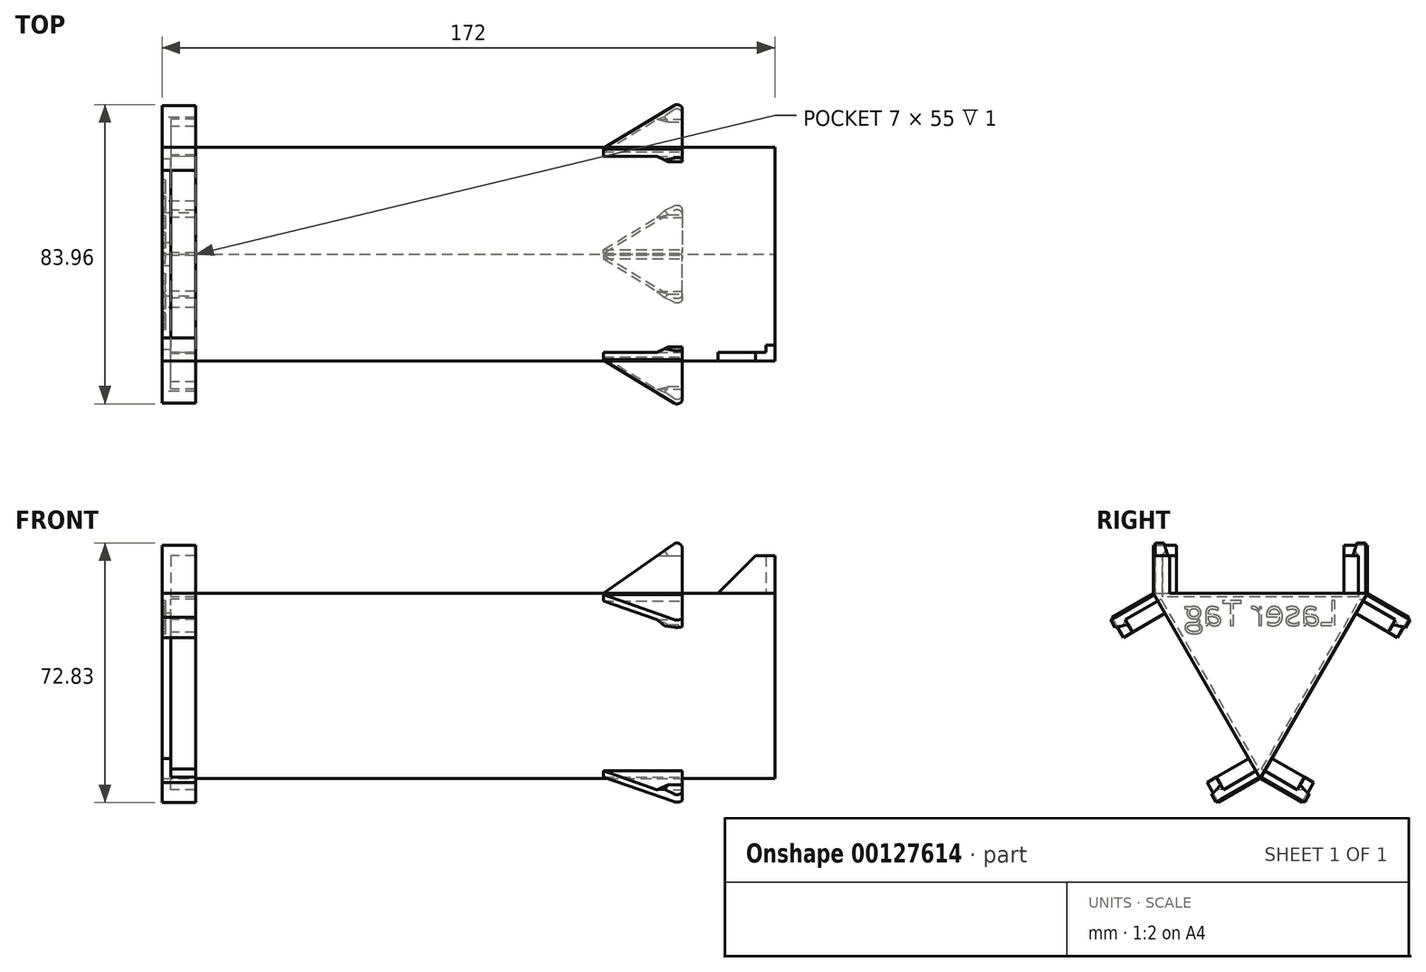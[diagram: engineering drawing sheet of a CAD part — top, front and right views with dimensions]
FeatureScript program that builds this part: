
annotation { "Feature Type Name" : "Feature", "Feature Type Description" : "" }
export const myFeature = defineFeature(function(context is Context, id is Id, definition is map)
    precondition{}
    {
        {
            var Q0;
            Q0=qCreatedBy(makeId("Top.planeOp"),FACE);
            var sketch = newSketch(context, id + "F0", { "sketchPlane" : qUnion([Q0])});
            skLineSegment(sketch, "E0.bottom", {"start": v(83.5, -27.5) * mm, "end": v(-83.5, -27.5) * mm, "construction": true});
            skLineSegment(sketch, "E0.top", {"start": v(83.5, 27.5) * mm, "end": v(-83.5, 27.5) * mm, "construction": true});
            skLineSegment(sketch, "E0.left", {"start": v(83.5, -27.5) * mm, "end": v(83.5, 27.5) * mm, "construction": true});
            skLineSegment(sketch, "E0.right", {"start": v(-83.5, -27.5) * mm, "end": v(-83.5, 27.5) * mm, "construction": true});
            skPoint(sketch, "E0.middle", {"position": v(0, 0) * mm});
            skLineSegment(sketch, "E1.bottom", {"start": v(86, -30) * mm, "end": v(-86, -30) * mm});
            skLineSegment(sketch, "E1.top", {"start": v(86, 0) * mm, "end": v(-86, 0) * mm});
            skLineSegment(sketch, "E1.left", {"start": v(86, -30) * mm, "end": v(86, 0) * mm});
            skLineSegment(sketch, "E1.right", {"start": v(-86, -30) * mm, "end": v(-86, 0) * mm});
            skPoint(sketch, "E1.middle", {"position": v(0, -15) * mm});
            skLineSegment(sketch, "E2", {"start": v(-83.5, -27.5) * mm, "end": v(-83.5, -30) * mm, "construction": true});
            skLineSegment(sketch, "E3", {"start": v(-83.5, -27.5) * mm, "end": v(-86, -27.5) * mm, "construction": true});
            skSolve(sketch);
        }
        {
            var Q0;
            Q0=qCreatedBy(makeId("Right.planeOp"),FACE);
            var Q1;
            Q1=sQuery(id+"F0.wireOp",VERTEX,"E1.top.start");
            cPlane(context, id + "F1", {"entities" : qUnion([Q0, Q1]), "cplaneType" : CPlaneType.PLANE_POINT, "offset" : 25 * mm, "width" : 150 * mm, "height" : 150 * mm});
        }
        {
            var Q0;
            Q0=qCreatedBy(id+"F1.planeOp",FACE);
            var sketch = newSketch(context, id + "F2", { "sketchPlane" : qUnion([Q0])});
            skCircle(sketch, "E4.cCircle", {"center": v(0, -17.32) * mm, "radius": 34.64 * mm, "construction": true});
            skLineSegment(sketch, "E4.0", {"start": v(30, 0) * mm, "end": v(0, -51.96) * mm});
            skLineSegment(sketch, "E4.1", {"start": v(0, -51.96) * mm, "end": v(-30, 0) * mm});
            skLineSegment(sketch, "E4.2", {"start": v(-30, 0) * mm, "end": v(30, 0) * mm});
            skLineSegment(sketch, "E5.0", {"start": v(-27.4, -1.5) * mm, "end": v(0, -1.5) * mm, "construction": true});
            skLineSegment(sketch, "E5.1", {"start": v(0, -48.96) * mm, "end": v(-13.7, -25.23) * mm, "construction": true});
            skLineSegment(sketch, "E5.2", {"start": v(27.4, -1.5) * mm, "end": v(0, -48.96) * mm, "construction": true});
            skLineSegment(sketch, "E6", {"start": v(0, -1.5) * mm, "end": v(-13.7, -25.23) * mm, "construction": true});
            skLineSegment(sketch, "E7", {"start": v(0, -1.5) * mm, "end": v(27.4, -1.5) * mm, "construction": true});
            skLineSegment(sketch, "E8", {"start": v(-13.7, -25.23) * mm, "end": v(-27.4, -1.5) * mm, "construction": true});
            skLineSegment(sketch, "E9", {"start": v(-13.7, -25.23) * mm, "end": v(-13.7, -9.41) * mm, "construction": true});
            skLineSegment(sketch, "E10", {"start": v(-27.4, -1.5) * mm, "end": v(-13.7, -9.41) * mm, "construction": true});
            skLineSegment(sketch, "E11", {"start": v(-13.7, -9.41) * mm, "end": v(-6.85, -13.37) * mm, "construction": true});
            skLineSegment(sketch, "E12", {"start": v(-13.7, -9.41) * mm, "end": v(-13.7, -1.5) * mm, "construction": true});
            skLineSegment(sketch, "E13", {"start": v(-27.4, -1.5) * mm, "end": v(-28.27, 0) * mm, "construction": true});
            skSolve(sketch);
        }
        {
            var Q0;
            Q0=qCreatedBy(makeId("Top.planeOp"),FACE);
            var Q1;
            Q1=sQuery(id+"F2.wireOp",VERTEX,"E4.cCircle.center");
            cPlane(context, id + "F3", {"entities" : qUnion([Q0, Q1]), "cplaneType" : CPlaneType.PLANE_POINT, "offset" : 25 * mm, "width" : 150 * mm, "height" : 150 * mm});
        }
        {
            var Q0;
            Q0=qCreatedBy(id+"F3.planeOp",FACE);
            var sketch = newSketch(context, id + "F4", { "sketchPlane" : qUnion([Q0])});
            skPoint(sketch, "E14.0", {"position": v(86, 0) * mm});
            skPoint(sketch, "E14.1", {"position": v(-86, 0) * mm});
            skLineSegment(sketch, "E15", {"start": v(86, 0) * mm, "end": v(-86, 0) * mm, "construction": true});
            skSolve(sketch);
        }
        {
            var Q0;
            Q0=qCreatedBy(makeId("Right.planeOp"),FACE);
            var Q1;
            Q1=sQuery(id+"F0.wireOp",VERTEX,"E1.top.end");
            cPlane(context, id + "F5", {"entities" : qUnion([Q0, Q1]), "cplaneType" : CPlaneType.PLANE_POINT, "offset" : 25 * mm, "width" : 150 * mm, "height" : 150 * mm});
        }
        {
            var Q0;
            Q0=makeQuery(id+"F2.imprint","IMPRINT",FACE,{"disambiguationData":[TD([[makeQuery(id+"F2.imprint","IMPRINT",EDGE,{"derivedFrom":sQuery(id+"F2.wireOp",EDGE,"E4.0")}),-1.0]])]});
            var Q1;
            Q1=qCreatedBy(id+"F5.planeOp",FACE);
            extrude(context, id + "F6", {"entities" : qUnion([Q0]), "endBound" : BoundingType.UP_TO_SURFACE, "oppositeDirection" : true, "endBoundEntityFace" : qUnion([Q1]), "depth" : 25 * mm});
        }
        {
            var Q0;
            Q0=makeQuery(id+"F6.opExtrude","SWEPT_FACE",FACE,{"disambiguationData":[OSD([sQuery(id+"F2.wireOp",EDGE,"E4.2")])]});
            var sketch = newSketch(context, id + "F7", { "sketchPlane" : qUnion([Q0])});
            skPoint(sketch, "E16.0", {"position": v(-83.5, -27.5) * mm});
            skPoint(sketch, "E17.0", {"position": v(83.5, -27.5) * mm});
            skLineSegment(sketch, "E18", {"start": v(-83.5, -27.5) * mm, "end": v(-83.5, -23.5) * mm});
            skLineSegment(sketch, "E19", {"start": v(-83.5, -23.5) * mm, "end": v(-86, -23.5) * mm});
            skLineSegment(sketch, "E20", {"start": v(-86, -23.5) * mm, "end": v(-86, -30) * mm});
            skLineSegment(sketch, "E21", {"start": v(-86, -30) * mm, "end": v(-76.5, -30) * mm});
            skLineSegment(sketch, "E22", {"start": v(-76.5, -30) * mm, "end": v(-76.5, -27.5) * mm});
            skLineSegment(sketch, "E23", {"start": v(-76.5, -27.5) * mm, "end": v(-83.5, -27.5) * mm});
            skLineSegment(sketch, "E24.bottom", {"start": v(83.5, -27.5) * mm, "end": v(80.5, -27.5) * mm});
            skLineSegment(sketch, "E24.top", {"start": v(86, -30) * mm, "end": v(80.5, -30) * mm});
            skLineSegment(sketch, "E24.right", {"start": v(80.5, -27.5) * mm, "end": v(80.5, -30) * mm});
            skLineSegment(sketch, "E25", {"start": v(83.5, -27.5) * mm, "end": v(83.5, -25.5) * mm});
            skLineSegment(sketch, "E26", {"start": v(83.5, -25.5) * mm, "end": v(86, -25.5) * mm});
            skLineSegment(sketch, "E27", {"start": v(86, -25.5) * mm, "end": v(86, -30) * mm});
            skSolve(sketch);
        }
        {
            var Q0;
            Q0=qSketchRegion(id+"F7",true);
            extrude(context, id + "F8", {"entities" : qUnion([Q0]), "depth" : 10.5 * mm});
        }
        {
            var Q0;
            Q0=makeQuery(id+"F8.opExtrude","CAP_FACE",FACE,{"disambiguationData":[OSD([sQuery(id+"F7.wireOp",EDGE,"E18"),sQuery(id+"F7.wireOp",EDGE,"E19"),sQuery(id+"F7.wireOp",EDGE,"E20"),sQuery(id+"F7.wireOp",EDGE,"E21"),sQuery(id+"F7.wireOp",EDGE,"E22"),sQuery(id+"F7.wireOp",EDGE,"E23")])],"isStart":false});
            var sketch = newSketch(context, id + "F9", { "sketchPlane" : qUnion([Q0])});
            skLineSegment(sketch, "E28.bottom", {"start": v(-86, -23.5) * mm, "end": v(-76.5, -23.5) * mm});
            skLineSegment(sketch, "E28.top", {"start": v(-86, -30) * mm, "end": v(-76.5, -30) * mm});
            skLineSegment(sketch, "E28.left", {"start": v(-86, -23.5) * mm, "end": v(-86, -30) * mm});
            skLineSegment(sketch, "E28.right", {"start": v(-76.5, -23.5) * mm, "end": v(-76.5, -30) * mm});
            skSolve(sketch);
        }
        {
            var Q0;
            Q0=qSketchRegion(id+"F9",true);
            extrude(context, id + "F10", {"entities" : qUnion([Q0]), "operationType" : NewBodyOperationType.ADD, "depth" : 3 * mm});
        }
        {
            var Q0;
            Q0=makeQuery(id+"F8.opExtrude","SWEPT_FACE",FACE,{"disambiguationData":[OSD([sQuery(id+"F7.wireOp",EDGE,"E24.top")])]});
            var sketch = newSketch(context, id + "F11", { "sketchPlane" : qUnion([Q0])});
            skLineSegment(sketch, "E29.0", {"start": v(80.5, 10.5) * mm, "end": v(80.5, 0) * mm});
            skLineSegment(sketch, "E30", {"start": v(80.5, 10.5) * mm, "end": v(70, 0) * mm});
            skLineSegment(sketch, "E31", {"start": v(70, 0) * mm, "end": v(80.5, 0) * mm});
            skSolve(sketch);
        }
        {
            var Q0;
            Q0=qSketchRegion(id+"F11",true);
            var Q1;
            Q1=makeQuery(id+"F8.opExtrude","SWEPT_FACE",FACE,{"disambiguationData":[OSD([sQuery(id+"F7.wireOp",EDGE,"E24.bottom")])]});
            extrude(context, id + "F12", {"entities" : qUnion([Q0]), "operationType" : NewBodyOperationType.ADD, "endBound" : BoundingType.UP_TO_SURFACE, "oppositeDirection" : true, "endBoundEntityFace" : qUnion([Q1]), "depth" : 25 * mm});
        }
        {
            var Q0;
            Q0=qCreatedBy(makeId("Front.planeOp"),FACE);
            var Q1;
            Q1=sQuery(id+"F0.wireOp",VERTEX,"E0.left.start");
            cPlane(context, id + "F13", {"entities" : qUnion([Q0, Q1]), "cplaneType" : CPlaneType.PLANE_POINT, "offset" : 25 * mm, "width" : 150 * mm, "height" : 150 * mm});
        }
        {
            var Q0;
            Q0=qCreatedBy(id+"F13.planeOp",FACE);
            var sketch = newSketch(context, id + "F14", { "sketchPlane" : qUnion([Q0])});
            skLineSegment(sketch, "E32.0", {"start": v(83.5, 0) * mm, "end": v(-83.5, 0) * mm, "construction": true});
            skLineSegment(sketch, "E33", {"start": v(37.86, 0) * mm, "end": v(60, 0) * mm});
            skLineSegment(sketch, "E34.0", {"start": v(70, 0) * mm, "end": v(80.5, 10.5) * mm, "construction": true});
            skLineSegment(sketch, "E35", {"start": v(37.86, 0) * mm, "end": v(60, 15.5) * mm});
            skLineSegment(sketch, "E36", {"start": v(60, 15.5) * mm, "end": v(60, 0) * mm});
            skLineSegment(sketch, "E37", {"start": v(80.5, 10.5) * mm, "end": v(60, 10.5) * mm, "construction": true});
            skSolve(sketch);
        }
        {
            var Q0;
            Q0=qSketchRegion(id+"F14",true);
            extrude(context, id + "F15", {"entities" : qUnion([Q0]), "depth" : 2 * mm});
        }
        {
            var Q0;
            Q0=makeQuery(id+"F15.opExtrude","SWEPT_FACE",FACE,{"disambiguationData":[OSD([sQuery(id+"F14.wireOp",EDGE,"E36")])]});
            var sketch = newSketch(context, id + "F16", { "sketchPlane" : qUnion([Q0])});
            skLineSegment(sketch, "E38.0", {"start": v(-27.5, 15.5) * mm, "end": v(-27.5, 0) * mm, "construction": true});
            skLineSegment(sketch, "E39", {"start": v(-27.5, 15.5) * mm, "end": v(-26, 10.5) * mm});
            skLineSegment(sketch, "E40", {"start": v(-26, 10.5) * mm, "end": v(-27.5, 10.5) * mm});
            skPoint(sketch, "E41.0", {"position": v(-27.5, 10.5) * mm});
            skLineSegment(sketch, "E42", {"start": v(-27.5, 10.5) * mm, "end": v(-27.5, 15.5) * mm});
            skSolve(sketch);
        }
        {
            var Q0;
            Q0=qSketchRegion(id+"F16",true);
            var Q1;
            Q1=makeQuery(id+"F15.opExtrude","SWEPT_FACE",FACE,{"disambiguationData":[OSD([sQuery(id+"F14.wireOp",EDGE,"E35")])]});
            extrude(context, id + "F17", {"entities" : qUnion([Q0]), "operationType" : NewBodyOperationType.ADD, "endBound" : BoundingType.UP_TO_SURFACE, "oppositeDirection" : true, "endBoundEntityFace" : qUnion([Q1]), "depth" : 25 * mm});
        }
        {
            var Q0;
            Q0=makeQuery(id+"F17.opExtrude","SWEPT_FACE",FACE,{"disambiguationData":[OSD([sQuery(id+"F16.wireOp",EDGE,"E40")])]});
            var sketch = newSketch(context, id + "F18", { "sketchPlane" : qUnion([Q0])});
            skLineSegment(sketch, "E43.0.0", {"start": v(52.86, 27.5) * mm, "end": v(52.86, 26) * mm, "construction": true});
            skLineSegment(sketch, "E43.0.1", {"start": v(52.86, 26) * mm, "end": v(60, 26) * mm, "construction": true});
            skLineSegment(sketch, "E43.0.2", {"start": v(60, 26) * mm, "end": v(60, 27.5) * mm, "construction": true});
            skLineSegment(sketch, "E43.0.3", {"start": v(60, 27.5) * mm, "end": v(52.86, 27.5) * mm, "construction": true});
            skLineSegment(sketch, "E44", {"start": v(52.86, 26) * mm, "end": v(52.86, 27.5) * mm});
            skLineSegment(sketch, "E45", {"start": v(52.86, 27.5) * mm, "end": v(56.08, 26) * mm});
            skLineSegment(sketch, "E46", {"start": v(56.08, 26) * mm, "end": v(52.86, 26) * mm});
            skSolve(sketch);
        }
        {
            var Q0;
            Q0=qSketchRegion(id+"F18",true);
            extrude(context, id + "F19", {"entities" : qUnion([Q0]), "operationType" : NewBodyOperationType.REMOVE, "endBound" : BoundingType.UP_TO_NEXT, "oppositeDirection" : true, "depth" : 25 * mm});
        }
        {
            var Q0;
            Q0=makeQuery(id+"F15.opExtrude","SWEPT_EDGE",EDGE,{"disambiguationData":[OSD([sQuery(id+"F14.wireOp",EDGE,"E35"),sQuery(id+"F14.wireOp",EDGE,"E36")])]});
            fillet(context, id + "F20", {"entities" : qUnion([Q0]), "radius" : 1.5 * mm, "tangentPropagation" : true, "allowEdgeOverflow" : false});
        }
        {
            var Q0;
            Q0=makeQuery(id+"F8.opExtrude","SWEPT_BODY",BODY,{"disambiguationData":[OSD([sQuery(id+"F7.wireOp",EDGE,"E18"),sQuery(id+"F7.wireOp",EDGE,"E19"),sQuery(id+"F7.wireOp",EDGE,"E20"),sQuery(id+"F7.wireOp",EDGE,"E21"),sQuery(id+"F7.wireOp",EDGE,"E22"),sQuery(id+"F7.wireOp",EDGE,"E23")])]});
            var Q1;
            Q1=makeQuery(id+"F8.opExtrude","SWEPT_BODY",BODY,{"disambiguationData":[OSD([sQuery(id+"F7.wireOp",EDGE,"E24.bottom"),sQuery(id+"F7.wireOp",EDGE,"E24.top"),sQuery(id+"F7.wireOp",EDGE,"E24.left"),sQuery(id+"F7.wireOp",EDGE,"E24.right")])]});
            var Q2;
            Q2=makeQuery(id+"F8.opExtrude","SWEPT_BODY",BODY,{"disambiguationData":[OSD([sQuery(id+"F7.wireOp",EDGE,"vPmypoo7-4PIT-Tpp9-nD1M-9n1DEz6bM5HR.bottom"),sQuery(id+"F7.wireOp",EDGE,"vPmypoo7-4PIT-Tpp9-nD1M-9n1DEz6bM5HR.top"),sQuery(id+"F7.wireOp",EDGE,"vPmypoo7-4PIT-Tpp9-nD1M-9n1DEz6bM5HR.left"),sQuery(id+"F7.wireOp",EDGE,"vPmypoo7-4PIT-Tpp9-nD1M-9n1DEz6bM5HR.right")])]});
            var Q3;
            Q3=makeQuery(id+"F15.opExtrude","SWEPT_BODY",BODY,{"disambiguationData":[OSD([sQuery(id+"F14.wireOp",EDGE,"E33"),sQuery(id+"F14.wireOp",EDGE,"E35"),sQuery(id+"F14.wireOp",EDGE,"5eTKJ0qs-JZWg-OuMg-Dukg-JtMXQiimBqfD"),sQuery(id+"F14.wireOp",EDGE,"rW7YqoKY-WMnB-SBIM-dDac-CuYA4JHaBWpu")])]});
            var Q4;
            Q4=qCreatedBy(makeId("Front.planeOp"),FACE);
            mirror(context, id + "F21", {"entities" : qUnion([Q0, Q1, Q2, Q3]), "mirrorPlane" : qUnion([Q4])});
        }
        {
            var Q0;
            Q0=makeQuery(id+"F8.opExtrude","SWEPT_BODY",BODY,{"disambiguationData":[OSD([sQuery(id+"F7.wireOp",EDGE,"E18"),sQuery(id+"F7.wireOp",EDGE,"E19"),sQuery(id+"F7.wireOp",EDGE,"E20"),sQuery(id+"F7.wireOp",EDGE,"E21"),sQuery(id+"F7.wireOp",EDGE,"E22"),sQuery(id+"F7.wireOp",EDGE,"E23")])]});
            var Q1;
            Q1=makeQuery(id+"F21.opPattern","COPY",BODY,{"derivedFrom":makeQuery(id+"F8.opExtrude","SWEPT_BODY",BODY,{"disambiguationData":[OSD([sQuery(id+"F7.wireOp",EDGE,"E18"),sQuery(id+"F7.wireOp",EDGE,"E19"),sQuery(id+"F7.wireOp",EDGE,"E20"),sQuery(id+"F7.wireOp",EDGE,"E21"),sQuery(id+"F7.wireOp",EDGE,"E22"),sQuery(id+"F7.wireOp",EDGE,"E23")])]}),"instanceName":"1"});
            var Q2;
            Q2=makeQuery(id+"F8.opExtrude","SWEPT_BODY",BODY,{"disambiguationData":[OSD([sQuery(id+"F7.wireOp",EDGE,"E24.bottom"),sQuery(id+"F7.wireOp",EDGE,"E24.top"),sQuery(id+"F7.wireOp",EDGE,"E24.left"),sQuery(id+"F7.wireOp",EDGE,"E24.right")])]});
            var Q3;
            Q3=makeQuery(id+"F8.opExtrude","SWEPT_BODY",BODY,{"disambiguationData":[OSD([sQuery(id+"F7.wireOp",EDGE,"vPmypoo7-4PIT-Tpp9-nD1M-9n1DEz6bM5HR.bottom"),sQuery(id+"F7.wireOp",EDGE,"vPmypoo7-4PIT-Tpp9-nD1M-9n1DEz6bM5HR.top"),sQuery(id+"F7.wireOp",EDGE,"vPmypoo7-4PIT-Tpp9-nD1M-9n1DEz6bM5HR.left"),sQuery(id+"F7.wireOp",EDGE,"vPmypoo7-4PIT-Tpp9-nD1M-9n1DEz6bM5HR.right")])]});
            var Q4;
            Q4=makeQuery(id+"F21.opPattern","COPY",BODY,{"derivedFrom":makeQuery(id+"F8.opExtrude","SWEPT_BODY",BODY,{"disambiguationData":[OSD([sQuery(id+"F7.wireOp",EDGE,"vPmypoo7-4PIT-Tpp9-nD1M-9n1DEz6bM5HR.bottom"),sQuery(id+"F7.wireOp",EDGE,"vPmypoo7-4PIT-Tpp9-nD1M-9n1DEz6bM5HR.top"),sQuery(id+"F7.wireOp",EDGE,"vPmypoo7-4PIT-Tpp9-nD1M-9n1DEz6bM5HR.left"),sQuery(id+"F7.wireOp",EDGE,"vPmypoo7-4PIT-Tpp9-nD1M-9n1DEz6bM5HR.right")])]}),"instanceName":"1"});
            var Q5;
            Q5=makeQuery(id+"F21.opPattern","COPY",BODY,{"derivedFrom":makeQuery(id+"F8.opExtrude","SWEPT_BODY",BODY,{"disambiguationData":[OSD([sQuery(id+"F7.wireOp",EDGE,"E24.bottom"),sQuery(id+"F7.wireOp",EDGE,"E24.top"),sQuery(id+"F7.wireOp",EDGE,"E24.left"),sQuery(id+"F7.wireOp",EDGE,"E24.right")])]}),"instanceName":"1"});
            var Q6;
            Q6=makeQuery(id+"F15.opExtrude","SWEPT_BODY",BODY,{"disambiguationData":[OSD([sQuery(id+"F14.wireOp",EDGE,"E33"),sQuery(id+"F14.wireOp",EDGE,"E35"),sQuery(id+"F14.wireOp",EDGE,"5eTKJ0qs-JZWg-OuMg-Dukg-JtMXQiimBqfD"),sQuery(id+"F14.wireOp",EDGE,"rW7YqoKY-WMnB-SBIM-dDac-CuYA4JHaBWpu")])]});
            var Q7;
            Q7=makeQuery(id+"F21.opPattern","COPY",BODY,{"derivedFrom":makeQuery(id+"F15.opExtrude","SWEPT_BODY",BODY,{"disambiguationData":[OSD([sQuery(id+"F14.wireOp",EDGE,"E33"),sQuery(id+"F14.wireOp",EDGE,"E35"),sQuery(id+"F14.wireOp",EDGE,"5eTKJ0qs-JZWg-OuMg-Dukg-JtMXQiimBqfD"),sQuery(id+"F14.wireOp",EDGE,"rW7YqoKY-WMnB-SBIM-dDac-CuYA4JHaBWpu")])]}),"instanceName":"1"});
            var Q8;
            Q8=sQuery(id+"F4.wireOp",EDGE,"E15");
            circularPattern(context, id + "F22", {"operationType" : NewBodyOperationType.ADD, "entities" : qUnion([Q0, Q1, Q2, Q3, Q4, Q5, Q6, Q7]), "axis" : qUnion([Q8]), "angle" : 120 * degree, "instanceCount" : 3, "computeTransformsWithoutBuiltin" : true});
        }
        {
            var Q0;
            Q0=makeQuery(id+"F6.opExtrude","SWEPT_FACE",FACE,{"disambiguationData":[OSD([sQuery(id+"F2.wireOp",EDGE,"E4.2")])]});
            var sketch = newSketch(context, id + "F23", { "sketchPlane" : qUnion([Q0])});
            skLineSegment(sketch, "E47.bottom", {"start": v(-83.5, 27.5) * mm, "end": v(-76.5, 27.5) * mm});
            skLineSegment(sketch, "E47.top", {"start": v(-83.5, -27.5) * mm, "end": v(-76.5, -27.5) * mm});
            skLineSegment(sketch, "E47.left", {"start": v(-83.5, 27.5) * mm, "end": v(-83.5, -27.5) * mm});
            skLineSegment(sketch, "E47.right", {"start": v(-76.5, 27.5) * mm, "end": v(-76.5, -27.5) * mm});
            skSolve(sketch);
        }
        {
            var Q0;
            Q0=qSketchRegion(id+"F23",true);
            extrude(context, id + "F24", {"entities" : qUnion([Q0]), "oppositeDirection" : true, "depth" : 1 * mm});
        }
        {
            var Q0;
            Q0=makeQuery(id+"F24.opExtrude","SWEPT_BODY",BODY,{"disambiguationData":[OSD([sQuery(id+"F23.wireOp",EDGE,"E47.bottom"),sQuery(id+"F23.wireOp",EDGE,"E47.top"),sQuery(id+"F23.wireOp",EDGE,"E47.left"),sQuery(id+"F23.wireOp",EDGE,"E47.right")])]});
            var Q1;
            Q1=sQuery(id+"F4.wireOp",EDGE,"E15");
            circularPattern(context, id + "F25", {"operationType" : NewBodyOperationType.REMOVE, "entities" : qUnion([Q0]), "axis" : qUnion([Q1]), "angle" : 120 * degree, "instanceCount" : 3, "computeTransformsWithoutBuiltin" : true});
        }
        {
            var Q0;
            {var subQ0=makeQuery(id+"F10.boolean.opBoolean","MERGE",FACE,{"derivedFrom":[makeQuery(id+"F8.opExtrude","SWEPT_FACE",FACE,{"disambiguationData":[OSD([sQuery(id+"F7.wireOp",EDGE,"E20")])]}),makeQuery(id+"F10.opExtrude","SWEPT_FACE",FACE,{"disambiguationData":[OSD([sQuery(id+"F9.wireOp",EDGE,"E28.left")])]})]});var subQ1=makeQuery(id+"F21.opPattern","COPY",FACE,{"derivedFrom":subQ0,"instanceName":"1"});Q0=makeQuery(id+"F22.boolean.opBoolean","MERGE",FACE,{"derivedFrom":[makeQuery(id+"F6.opExtrude","CAP_FACE",FACE,{"disambiguationData":[OSD([dummyQuery(id+"F5.planeOp",FACE)])],"isStart":false}),subQ0,subQ1,makeQuery(id+"F22.opPattern","COPY",FACE,{"derivedFrom":subQ0,"instanceName":"1"}),makeQuery(id+"F22.opPattern","COPY",FACE,{"derivedFrom":subQ1,"instanceName":"1"}),makeQuery(id+"F22.opPattern","COPY",FACE,{"derivedFrom":subQ0,"instanceName":"2"}),makeQuery(id+"F22.opPattern","COPY",FACE,{"derivedFrom":subQ1,"instanceName":"2"})]});}
            var sketch = newSketch(context, id + "F26", { "sketchPlane" : qUnion([Q0])});
            skText(sketch, "E48", { "text": "Laser Tag", "fontName": "OpenSans-Regular.ttf"});
            skLineSegment(sketch, "E49", {"start": v(-21.4, -8.88) * mm, "end": v(-24, -10.38) * mm, "construction": true});
            skLineSegment(sketch, "E50", {"start": v(21.4, -8.88) * mm, "end": v(24, -10.38) * mm, "construction": true});
            const initialGuessF26  = {"E48": [-0.02183, -0.00902, 1, 0, 0.00702]};
            skSetInitialGuess(sketch, initialGuessF26);
            skSolve(sketch);
        }
        {
            var Q0;
            Q0=qSketchRegion(id+"F26",true);
            extrude(context, id + "F27", {"entities" : qUnion([Q0]), "operationType" : NewBodyOperationType.REMOVE, "oppositeDirection" : true, "depth" : 1 * mm});
        }
    });
